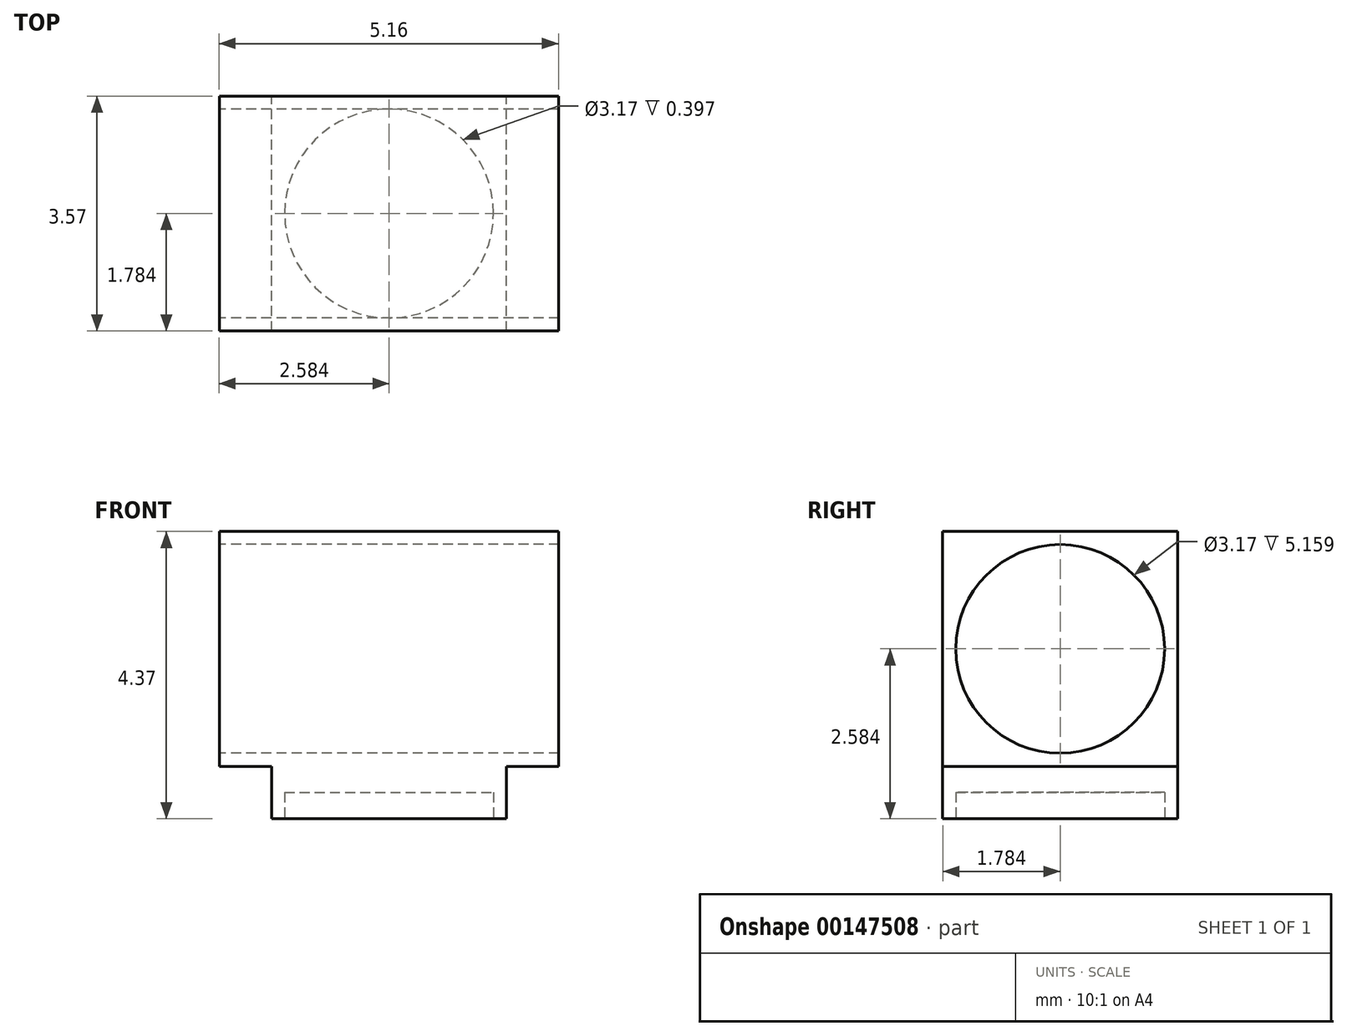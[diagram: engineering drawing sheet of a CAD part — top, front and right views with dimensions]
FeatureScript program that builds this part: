
annotation { "Feature Type Name" : "Feature", "Feature Type Description" : "" }
export const myFeature = defineFeature(function(context is Context, id is Id, definition is map)
    precondition{}
    {
        {
            var Q0;
            Q0=qCreatedBy(makeId("Front.planeOp"),FACE);
            var sketch = newSketch(context, id + "F0", { "sketchPlane" : qUnion([Q0])});
            skLineSegment(sketch, "E0", {"start": v(0, 1.93) * mm, "end": v(-3.57, 1.93) * mm});
            skLineSegment(sketch, "E1", {"start": v(-3.57, 1.93) * mm, "end": v(-3.57, 2.73) * mm});
            skLineSegment(sketch, "E2", {"start": v(0, 1.93) * mm, "end": v(0, 2.73) * mm});
            skLineSegment(sketch, "E3", {"start": v(0, 2.73) * mm, "end": v(0.8, 2.73) * mm});
            skLineSegment(sketch, "E4", {"start": v(0.8, 2.73) * mm, "end": v(0.8, 6.3) * mm});
            skLineSegment(sketch, "E5", {"start": v(0.8, 6.3) * mm, "end": v(-4.37, 6.3) * mm});
            skLineSegment(sketch, "E6", {"start": v(-3.57, 2.73) * mm, "end": v(-4.37, 2.73) * mm});
            skLineSegment(sketch, "E7", {"start": v(-4.37, 6.3) * mm, "end": v(-4.37, 2.73) * mm});
            skSolve(sketch);
        }
        {
            var Q0;
            Q0 = qSketchRegion(id + "F0", true);
            extrude(context, id + "F1", {"entities" : qUnion([Q0]), "depth" : 3.57 * mm});
        }
        {
            var Q0;
            Q0=makeQuery(id+"F1.opExtrude","SWEPT_FACE",FACE,{"disambiguationData":[OSD([sQuery(id+"F0.wireOp",EDGE,"E0")])]});
            var sketch = newSketch(context, id + "F2", { "sketchPlane" : qUnion([Q0])});
            skCircle(sketch, "E8", {"center": v(-1.79, 1.79) * mm, "radius": 1.59 * mm});
            skPoint(sketch, "E8.centerSnap0", {"position": v(0, 1.79) * mm});
            skPoint(sketch, "E8.centerSnap1", {"position": v(-1.79, 0) * mm});
            skSolve(sketch);
        }
        {
            var Q0;
            Q0 = qSketchRegion(id + "F2", true);
            extrude(context, id + "F3", {"entities" : qUnion([Q0]), "operationType" : NewBodyOperationType.REMOVE, "oppositeDirection" : true, "depth" : 0.4 * mm});
        }
        {
            var Q0;
            Q0=makeQuery(id+"F1.opExtrude","SWEPT_FACE",FACE,{"disambiguationData":[OSD([sQuery(id+"F0.wireOp",EDGE,"E7")])]});
            var sketch = newSketch(context, id + "F4", { "sketchPlane" : qUnion([Q0])});
            skCircle(sketch, "E9", {"center": v(1.79, 4.51) * mm, "radius": 1.59 * mm});
            skPoint(sketch, "E9.centerSnap0", {"position": v(1.79, 6.3) * mm});
            skPoint(sketch, "E9.centerSnap1", {"position": v(3.57, 4.51) * mm});
            skSolve(sketch);
        }
        {
            var Q0;
            Q0 = qSketchRegion(id + "F4", true);
            extrude(context, id + "F5", {"entities" : qUnion([Q0]), "operationType" : NewBodyOperationType.REMOVE, "oppositeDirection" : true, "depth" : 25.4 * mm});
        }
    });
